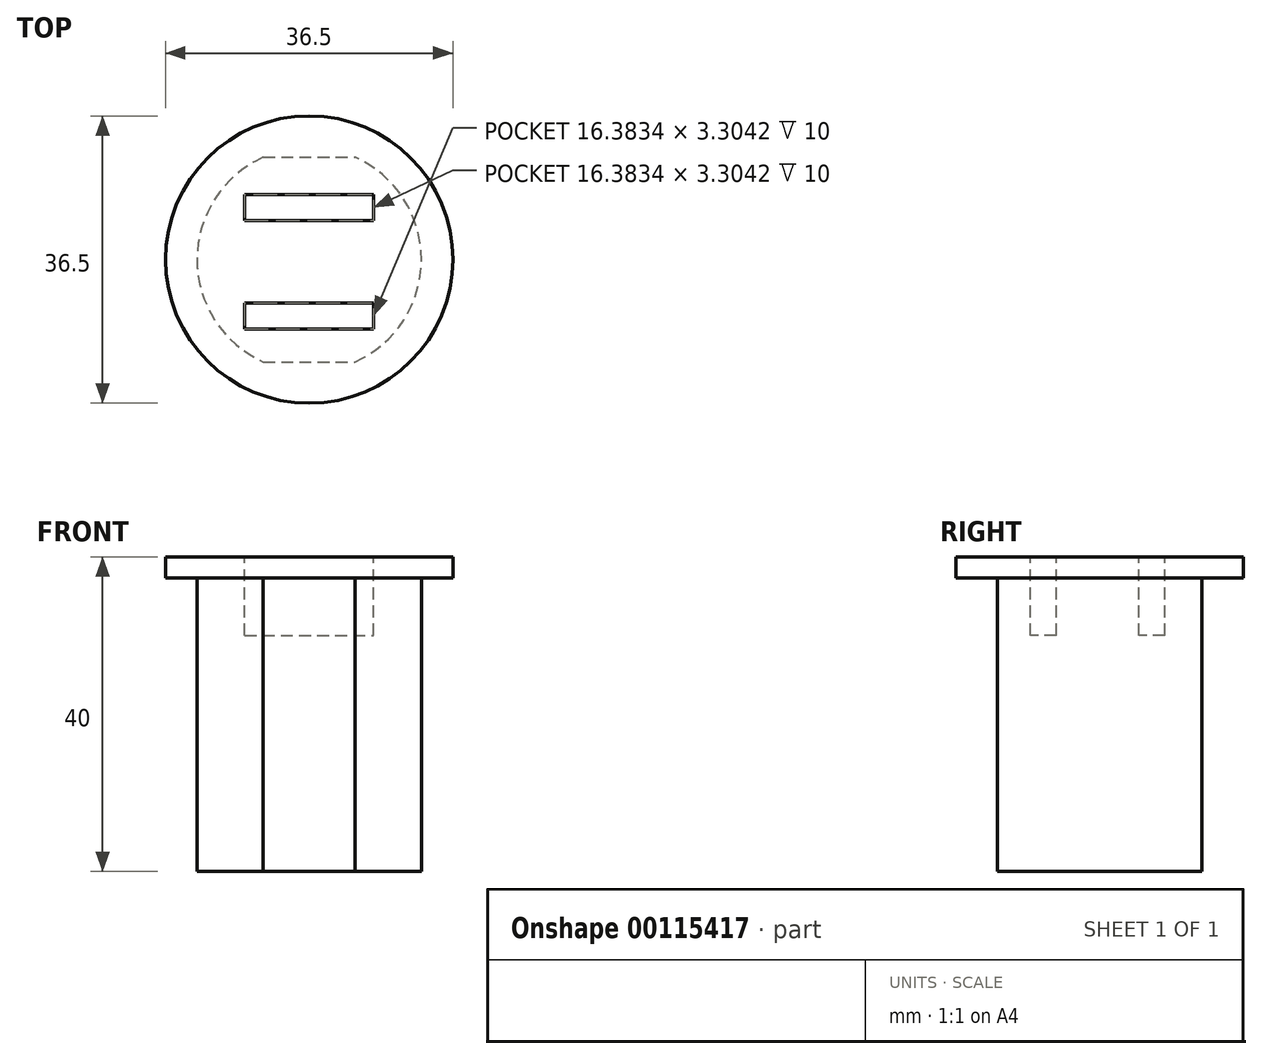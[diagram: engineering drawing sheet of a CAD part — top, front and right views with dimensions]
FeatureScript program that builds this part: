
annotation { "Feature Type Name" : "Feature", "Feature Type Description" : "" }
export const myFeature = defineFeature(function(context is Context, id is Id, definition is map)
    precondition{}
    {
        {
            var Q0;
            Q0=qCreatedBy(makeId("Front.planeOp"),FACE);
            var sketch = newSketch(context, id + "F0", { "sketchPlane" : qUnion([Q0])});
            skLineSegment(sketch, "E0", {"start": v(0, 2.7) * mm, "end": v(-18.25, 2.7) * mm});
            skLineSegment(sketch, "E1", {"start": v(-18.25, 2.7) * mm, "end": v(-18.25, 0) * mm});
            skLineSegment(sketch, "E2", {"start": v(-18.25, 0) * mm, "end": v(-14.25, 0) * mm});
            skLineSegment(sketch, "E3", {"start": v(-14.25, 0) * mm, "end": v(-14.25, -37.3) * mm});
            skLineSegment(sketch, "E4", {"start": v(-14.25, -37.3) * mm, "end": v(0, -37.3) * mm});
            skLineSegment(sketch, "E5", {"start": v(0, -37.3) * mm, "end": v(0, 2.7) * mm});
            skSolve(sketch);
        }
        {
            var Q0;
            Q0=qSketchRegion(id+"F0",true);
            var Q1;
            Q1=sQuery(id+"F0.wireOp",EDGE,"E5");
            revolve(context, id + "F1", {"entities" : qUnion([Q0]), "axis" : qUnion([Q1]), "revolveType" : RevolveType.FULL});
        }
        {
            var Q0;
            Q0=makeQuery(id+"F1.opRevolve","SWEPT_FACE",FACE,{"disambiguationData":[OSD([sQuery(id+"F0.wireOp",EDGE,"E0")])]});
            var sketch = newSketch(context, id + "F2", { "sketchPlane" : qUnion([Q0])});
            skLineSegment(sketch, "E6.bottom", {"start": v(-8.2, 8.26) * mm, "end": v(8.2, 8.26) * mm});
            skLineSegment(sketch, "E6.top", {"start": v(-8.2, 4.96) * mm, "end": v(8.2, 4.96) * mm});
            skLineSegment(sketch, "E6.left", {"start": v(-8.2, 8.26) * mm, "end": v(-8.2, 4.96) * mm});
            skLineSegment(sketch, "E6.right", {"start": v(8.2, 8.26) * mm, "end": v(8.2, 4.96) * mm});
            skLineSegment(sketch, "E7.bottom", {"start": v(-8.2, -5.5) * mm, "end": v(8.2, -5.5) * mm});
            skLineSegment(sketch, "E7.top", {"start": v(-8.2, -8.81) * mm, "end": v(8.2, -8.81) * mm});
            skLineSegment(sketch, "E7.left", {"start": v(-8.2, -5.5) * mm, "end": v(-8.2, -8.81) * mm});
            skLineSegment(sketch, "E7.right", {"start": v(8.2, -5.5) * mm, "end": v(8.2, -8.81) * mm});
            skLineSegment(sketch, "E8", {"start": v(0, 18.25) * mm, "end": v(0, 8.26) * mm, "construction": true});
            skLineSegment(sketch, "E9", {"start": v(0, 4.96) * mm, "end": v(0, -5.5) * mm, "construction": true});
            skLineSegment(sketch, "E10", {"start": v(0, -8.81) * mm, "end": v(0, -18.25) * mm, "construction": true});
            skSolve(sketch);
        }
        {
            var Q0;
            Q0=qSketchRegion(id+"F2",true);
            extrude(context, id + "F3", {"entities" : qUnion([Q0]), "operationType" : NewBodyOperationType.REMOVE, "oppositeDirection" : true, "depth" : 10 * mm});
        }
        {
            var Q0;
            Q0=makeQuery(id+"F1.opRevolve","SWEPT_FACE",FACE,{"disambiguationData":[OSD([sQuery(id+"F0.wireOp",EDGE,"E4")])]});
            var sketch = newSketch(context, id + "F4", { "sketchPlane" : qUnion([Q0])});
            skArc(sketch, "E11.0", {"start": v(-5.84, -13) * mm, "mid": v(0, -14.25) * mm, "end": v(5.84, -13) * mm});
            skLineSegment(sketch, "E12", {"start": v(-5.84, 13) * mm, "end": v(5.84, 13) * mm});
            skLineSegment(sketch, "E13.MirrorCS", {"start": v(-5.84, -13) * mm, "end": v(5.84, -13) * mm});
            skArc(sketch, "E14.trimOffspring", {"start": v(5.84, 13) * mm, "mid": v(0, 14.25) * mm, "end": v(-5.84, 13) * mm});
            skSolve(sketch);
        }
        {
            var Q0;
            Q0=makeQuery(id+"F4.imprint","IMPRINT",FACE,{"disambiguationData":[TD([[makeQuery(id+"F4.imprint","IMPRINT",EDGE,{"derivedFrom":sQuery(id+"F4.wireOp",EDGE,"E12")}),1.0]])]});
            var Q1;
            Q1=makeQuery(id+"F4.imprint","IMPRINT",FACE,{"disambiguationData":[TD([[makeQuery(id+"F4.imprint","IMPRINT",EDGE,{"derivedFrom":sQuery(id+"F4.wireOp",EDGE,"E11.0")}),1.0]])]});
            var Q2;
            Q2=makeQuery(id+"F1.opRevolve","SWEPT_FACE",FACE,{"disambiguationData":[OSD([sQuery(id+"F0.wireOp",EDGE,"E2")])]});
            extrude(context, id + "F5", {"entities" : qUnion([Q0, Q1]), "operationType" : NewBodyOperationType.REMOVE, "endBound" : BoundingType.UP_TO_SURFACE, "oppositeDirection" : true, "endBoundEntityFace" : qUnion([Q2]), "depth" : 25 * mm});
        }
    });
